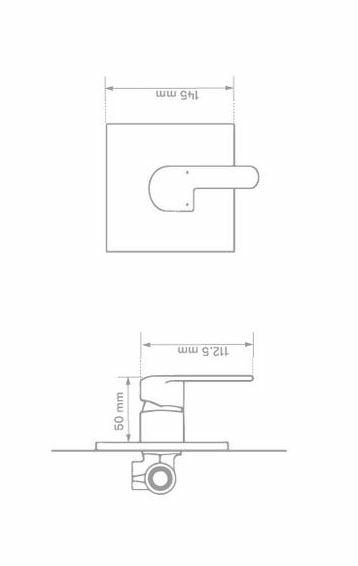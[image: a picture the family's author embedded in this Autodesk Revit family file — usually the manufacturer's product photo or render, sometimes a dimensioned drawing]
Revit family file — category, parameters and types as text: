
# Revit family: 01-0933-11 REGISTRO DUCHA HELVETIA
name_source: partatom
category: Plumbing Fixtures
revit_build: Autodesk Revit 2018 (Build: 20170223_1515(x64)
units: mm (PartAtom-declared; Revit-internal decimal feet)

## family parameters
Cut with Voids When Loaded = No
Host = Face
OmniClass Number = 23.31.11.00
Part Type = Normal
Room Calculation Point = No
Round Connector Dimension = Use Diameter
Shared = No

## types (1)
- 01-0933-11
    Alto = 85 mm  [stored 0.278871 ft]
    Ancho manija = 70 mm
    CW Connection = Yes
    Default Elevation = 0 mm  [stored 0 ft]
    Description = Registro
    Dim escudo = 60 mm
    HW Connection = Yes
    Link Ficha Tecnica = http://infotecnica.gricol.com
    Manufacturer = Gricol
    Model = 01-0933-11
    Plastico - ABS Cromado = Plastico - ABS Cromado
    Product Name = REGISTRO DUCHA HELVETIA
    Type Image = REGISTRO DUCHA HELVETIA.jpg
    URL = https://www.gricol.com
    Vent Connection = No
    Waste Connection = No

note: [stored X ft] marks values corroborated as IEEE doubles in the binary element streams (Revit-internal decimal feet)

## geometry (parser evidence)
native form markers: Blend x2, Sweep x7
no freeform markers — native parametric forms only
